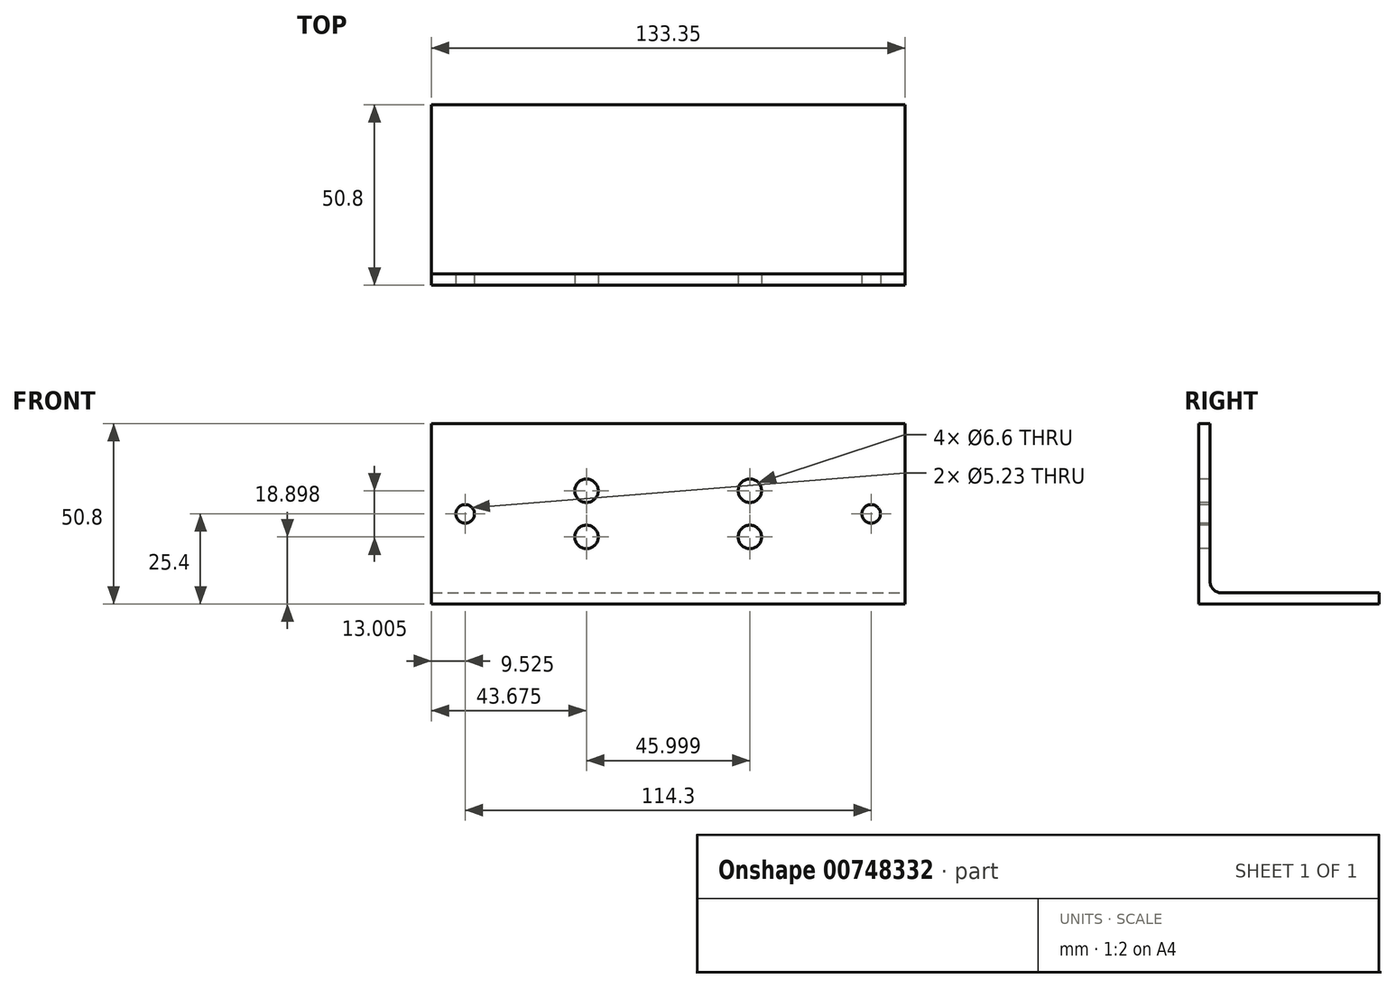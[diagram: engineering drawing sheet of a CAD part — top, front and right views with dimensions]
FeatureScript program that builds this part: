
annotation { "Feature Type Name" : "Feature", "Feature Type Description" : "" }
export const myFeature = defineFeature(function(context is Context, id is Id, definition is map)
    precondition{}
    {
        {
            var Q0;
            Q0=qCreatedBy(makeId("Right.planeOp"),FACE);
            var sketch = newSketch(context, id + "F0", { "sketchPlane" : qUnion([Q0])});
            skLineSegment(sketch, "E0", {"start": v(0, 0) * mm, "end": v(0, -44.45) * mm});
            skLineSegment(sketch, "E1", {"start": v(3.18, -47.62) * mm, "end": v(47.63, -47.62) * mm});
            skLineSegment(sketch, "E2.0", {"start": v(-3.18, -50.8) * mm, "end": v(47.63, -50.8) * mm});
            skLineSegment(sketch, "E2.1", {"start": v(-3.17, 0) * mm, "end": v(-3.18, -50.8) * mm});
            skLineSegment(sketch, "E3", {"start": v(-3.18, 0) * mm, "end": v(0, 0) * mm});
            skLineSegment(sketch, "E4", {"start": v(47.63, -47.62) * mm, "end": v(47.63, -50.8) * mm});
            skPoint(sketch, "E5.visualSharp", {"position": v(0, -47.63) * mm});
            skArc(sketch, "E5.filletArc", {"start": v(0, -44.45) * mm, "mid": v(0.93, -46.7) * mm, "end": v(3.18, -47.63) * mm});
            skSolve(sketch);
        }
        {
            var Q0;
            Q0=makeQuery(id+"F0.imprint","IMPRINT",FACE,{"disambiguationData":[TD([[makeQuery(id+"F0.imprint","IMPRINT",EDGE,{"derivedFrom":sQuery(id+"F0.wireOp",EDGE,"E0")}),-1.0]])]});
            extrude(context, id + "F1", {"entities" : qUnion([Q0]), "oppositeDirection" : true, "depth" : 133.35 * mm, "offsetDistance" : 25.4 * mm});
        }
        {
            var Q0;
            Q0=makeQuery(id+"F1.opExtrude","SWEPT_FACE",FACE,{"disambiguationData":[OSD([sQuery(id+"F0.wireOp",EDGE,"E2.1")])]});
            var sketch = newSketch(context, id + "F2", { "sketchPlane" : qUnion([Q0])});
            skLineSegment(sketch, "E6", {"start": v(0, -25.4) * mm, "end": v(-133.35, -25.4) * mm, "construction": true});
            skLineSegment(sketch, "E7", {"start": v(-66.68, 0) * mm, "end": v(-66.68, -50.8) * mm, "construction": true});
            skLineSegment(sketch, "E8.0", {"start": v(-123.83, 0) * mm, "end": v(-123.83, -50.8) * mm, "construction": true});
            skLineSegment(sketch, "E9.0", {"start": v(-9.53, 0) * mm, "end": v(-9.53, -50.8) * mm, "construction": true});
            skCircle(sketch, "E10", {"center": v(-123.83, -25.4) * mm, "radius": 2.62 * mm});
            skCircle(sketch, "E11", {"center": v(-9.53, -25.4) * mm, "radius": 2.62 * mm});
            skLineSegment(sketch, "E12.bottom", {"start": v(-43.68, -18.9) * mm, "end": v(-89.67, -18.9) * mm, "construction": true});
            skLineSegment(sketch, "E12.top", {"start": v(-43.68, -31.9) * mm, "end": v(-89.67, -31.9) * mm, "construction": true});
            skLineSegment(sketch, "E12.left", {"start": v(-43.68, -18.9) * mm, "end": v(-43.68, -31.9) * mm, "construction": true});
            skLineSegment(sketch, "E12.right", {"start": v(-89.67, -18.9) * mm, "end": v(-89.67, -31.9) * mm, "construction": true});
            skPoint(sketch, "E12.middle", {"position": v(-66.67, -25.4) * mm});
            skCircle(sketch, "E13", {"center": v(-89.67, -18.9) * mm, "radius": 3.3 * mm});
            skCircle(sketch, "E14", {"center": v(-89.67, -31.9) * mm, "radius": 3.3 * mm});
            skCircle(sketch, "E15", {"center": v(-43.68, -18.9) * mm, "radius": 3.3 * mm});
            skCircle(sketch, "E16", {"center": v(-43.68, -31.9) * mm, "radius": 3.3 * mm});
            skSolve(sketch);
        }
        {
            var Q0;
            Q0=qSketchRegion(id+"F2",true);
            extrude(context, id + "F3", {"entities" : qUnion([Q0]), "operationType" : NewBodyOperationType.REMOVE, "endBound" : BoundingType.THROUGH_ALL, "oppositeDirection" : true, "depth" : 25.4 * mm, "offsetDistance" : 25.4 * mm});
        }
    });
